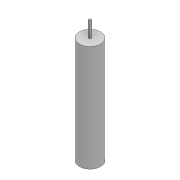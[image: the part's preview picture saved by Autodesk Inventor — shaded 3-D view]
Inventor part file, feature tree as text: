
AUTODESK INVENTOR PART (.ipt)
format: ipt  version: 2017 (Build 210142000, 142)  size: 82,944 bytes
history: native  units: mm
features: sketch x3, extrude x2
ambient origin geometry x8: Origin, YZ Plane, XZ Plane, XY Plane, X Axis, Y Axis, Z Axis, Center Point
bodies: Solid1 (feature_tree)
feature tree (5):
  extrude  "Extrusion1"  Depth=10.0mm TaperAngle=0.0deg
  extrude  "Extrusion2"  Depth=1.5mm
  sketch  "Sketch3"  dims[d6=100.0mm]
  sketch  "Sketch1"  dims[d0=2.0mm d1=10.0mm d2=0.0mm]
  sketch  "Sketch2"  dims[d3=1.5mm d4=0.0mm d5=100.0mm]
